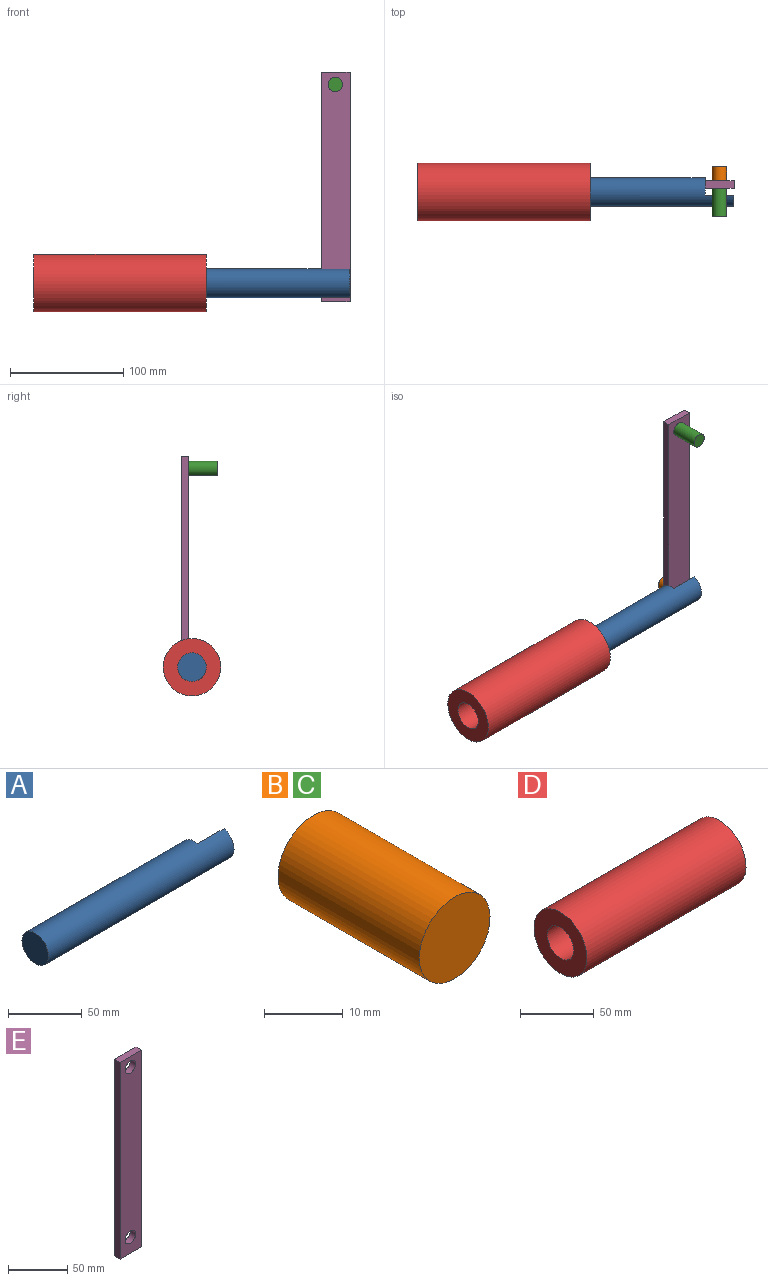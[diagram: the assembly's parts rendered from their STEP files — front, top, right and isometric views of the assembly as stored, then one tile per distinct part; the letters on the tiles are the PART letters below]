
ASSEMBLY  parts=5 mates=4
PART A: 5 faces, bbox 177.8x25.4x25.4 mm
  f0: cylinder r=12.7mm len=177.8mm, axis (1,0,0), area 13011.4mm2, adj f1,f2,f3,f4
  f1: plane 25.4x25.4mm, normal (-1,0,0), area 506.7mm2, adj f0
  f2: plane 25.4x15.88mm, normal (1,0,0), area 333.2mm2, adj f0,f3
  f3: plane 25.4x24.59mm, normal (0,1,0), area 624.7mm2, adj f0,f2,f4
  f4: plane 24.59x9.53mm, normal (1,0,0), area 173.6mm2, adj f0,f3
PART B: 3 faces, bbox 12.7x25.4x12.7 mm
  f0: cylinder r=6.35mm len=25.4mm, axis (0,1,0), area 1013.4mm2, adj f1,f2
  f1: plane 12.7x12.7mm, normal (0,-1,0), area 126.7mm2, adj f0
  f2: plane 12.7x12.7mm, normal (0,1,0), area 126.7mm2, adj f0
PART C: same geometry as B
PART D: 4 faces, bbox 152.4x50.8x50.8 mm
  f0: cylinder r=12.7mm len=152.4mm, axis (1,0,0), area 12161mm2, adj f2,f3
  f1: cylinder r=25.4mm len=152.4mm, axis (1,0,0), area 24322mm2, adj f2,f3
  f2: plane 50.8x50.8mm, normal (-1,0,0), area 1520.1mm2, adj f0,f1
  f3: plane 50.8x50.8mm, normal (1,0,0), area 1520.1mm2, adj f0,f1
PART E: 8 faces, bbox 25.4x6.4x203.2 mm
  f0: plane 25.4x6.35mm, normal (0,0,1), area 161.3mm2, adj f1,f5,f6,f7
  f1: plane 203.2x6.35mm, normal (-1,0,0), area 1290.3mm2, adj f0,f2,f6,f7
  f2: plane 25.4x6.35mm, normal (0,0,-1), area 161.3mm2, adj f1,f5,f6,f7
  f3: cylinder r=6.35mm len=12.7mm, axis (0,1,0), area 253.4mm2, adj f6,f7
  f4: cylinder r=6.35mm len=12.7mm, axis (0,1,0), area 253.4mm2, adj f6,f7
  f5: plane 203.2x6.35mm, normal (1,0,0), area 1290.3mm2, adj f0,f2,f6,f7
  f6: plane 203.2x25.4mm, normal (0,-1,0), area 4907.9mm2, adj f0,f1,f2,f3,f4,f5
  f7: plane 203.2x25.4mm, normal (0,1,0), area 4907.9mm2, adj f0,f1,f2,f3,f4,f5
PLACE A t=(-20.49,1.89,40.1)mm
PLACE B t=(-20.17,11.41,40.1)mm
PLACE C t=(-20.17,-7.64,215.96)mm fixed
PLACE D t=(30.31,1.89,40.1)mm fixed
PLACE E t=(-20.17,8.24,40.1)mm
MATE cylindrical B.f0 <-> A.f3  axis (0,1,0) through (-20.17,-1.29,40.1)mm
MATE revolute E.f4 <-> B.f0  axis (0,1,0) through (-20.17,11.41,40.1)mm
MATE revolute C.f0 <-> E.f3  axis (0,1,0) through (-20.17,5.06,215.96)mm
MATE slider A.f0 <-> D.f1  axis (-1,0,0) through (-185.27,1.89,40.1)mm
